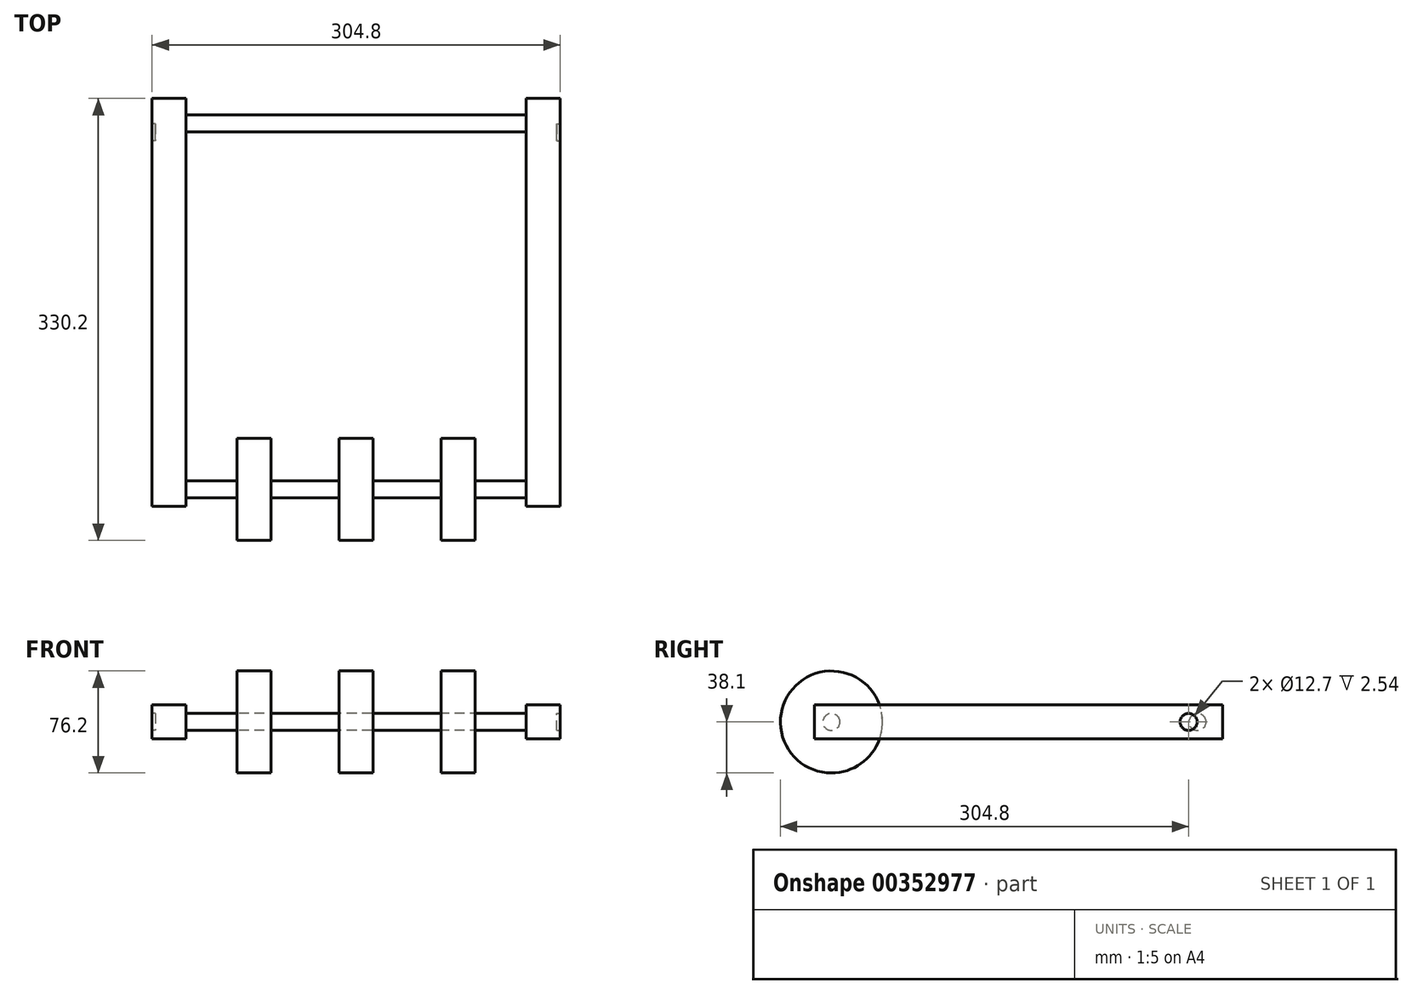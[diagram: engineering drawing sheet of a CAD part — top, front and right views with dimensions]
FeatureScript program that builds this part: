
annotation { "Feature Type Name" : "Feature", "Feature Type Description" : "" }
export const myFeature = defineFeature(function(context is Context, id is Id, definition is map)
    precondition{}
    {
        {
            var Q0;
            Q0=qCreatedBy(makeId("Front.planeOp"),FACE);
            var sketch = newSketch(context, id + "F0", { "sketchPlane" : qUnion([Q0])});
            skLineSegment(sketch, "E0.bottom", {"start": v(-127, -12.7) * mm, "end": v(-152.4, -12.7) * mm});
            skLineSegment(sketch, "E0.top", {"start": v(-127, 12.7) * mm, "end": v(-152.4, 12.7) * mm});
            skLineSegment(sketch, "E0.left", {"start": v(-127, -12.7) * mm, "end": v(-127, 12.7) * mm});
            skLineSegment(sketch, "E0.right", {"start": v(-152.4, -12.7) * mm, "end": v(-152.4, 12.7) * mm});
            skPoint(sketch, "E0.middle", {"position": v(-139.7, 0) * mm});
            skLineSegment(sketch, "E1.bottom", {"start": v(152.4, -12.7) * mm, "end": v(127, -12.7) * mm});
            skLineSegment(sketch, "E1.top", {"start": v(152.4, 12.7) * mm, "end": v(127, 12.7) * mm});
            skLineSegment(sketch, "E1.left", {"start": v(152.4, -12.7) * mm, "end": v(152.4, 12.7) * mm});
            skLineSegment(sketch, "E1.right", {"start": v(127, -12.7) * mm, "end": v(127, 12.7) * mm});
            skPoint(sketch, "E1.middle", {"position": v(139.7, 0) * mm});
            skSolve(sketch);
        }
        {
            var Q0;
            Q0 = qSketchRegion(id + "F0", true);
            extrude(context, id + "F1", {"entities" : qUnion([Q0]), "oppositeDirection" : true, "depth" : 25.4 * mm, "hasSecondDirection" : true, "secondDirectionOppositeDirection" : false, "secondDirectionDepth" : 279.4 * mm});
        }
        {
            var Q0;
            Q0=makeQuery(id+"F1.opExtrude","SWEPT_FACE",FACE,{"disambiguationData":[OSD([sQuery(id+"F0.wireOp",EDGE,"E0.right")])]});
            var sketch = newSketch(context, id + "F2", { "sketchPlane" : qUnion([Q0])});
            skCircle(sketch, "E2", {"center": v(0, 0) * mm, "radius": 6.35 * mm});
            skSolve(sketch);
        }
        {
            var Q0;
            Q0=makeQuery(id+"F1.opExtrude","SWEPT_FACE",FACE,{"disambiguationData":[OSD([sQuery(id+"F0.wireOp",EDGE,"E1.left")])]});
            var sketch = newSketch(context, id + "F3", { "sketchPlane" : qUnion([Q0])});
            skCircle(sketch, "E3", {"center": v(0, 0) * mm, "radius": 6.35 * mm});
            skSolve(sketch);
        }
        {
            var Q0;
            Q0 = qSketchRegion(id + "F2", true);
            extrude(context, id + "F4", {"entities" : qUnion([Q0]), "operationType" : NewBodyOperationType.REMOVE, "oppositeDirection" : true, "depth" : 2.54 * mm});
        }
        {
            var Q0;
            Q0 = qSketchRegion(id + "F3", true);
            extrude(context, id + "F5", {"entities" : qUnion([Q0]), "operationType" : NewBodyOperationType.REMOVE, "oppositeDirection" : true, "depth" : 2.54 * mm});
        }
        {
            var Q0;
            Q0=makeQuery(id+"F1.opExtrude","SWEPT_FACE",FACE,{"disambiguationData":[OSD([sQuery(id+"F0.wireOp",EDGE,"E0.left")])]});
            var sketch = newSketch(context, id + "F6", { "sketchPlane" : qUnion([Q0])});
            skCircle(sketch, "E4", {"center": v(6.7, 0) * mm, "radius": 6.35 * mm});
            skSolve(sketch);
        }
        {
            var Q0;
            Q0 = qSketchRegion(id + "F6", true);
            extrude(context, id + "F7", {"entities" : qUnion([Q0]), "depth" : 254 * mm});
        }
        {
            var Q0;
            Q0=makeQuery(id+"F1.opExtrude","SWEPT_FACE",FACE,{"disambiguationData":[OSD([sQuery(id+"F0.wireOp",EDGE,"E0.left")])]});
            var sketch = newSketch(context, id + "F8", { "sketchPlane" : qUnion([Q0])});
            skCircle(sketch, "E5", {"center": v(-266.7, 0) * mm, "radius": 6.35 * mm});
            skSolve(sketch);
        }
        {
            var Q0;
            Q0 = qSketchRegion(id + "F8", true);
            extrude(context, id + "F9", {"entities" : qUnion([Q0]), "depth" : 254 * mm});
        }
        {
            var Q0;
            Q0=qCreatedBy(makeId("Right.planeOp"),FACE);
            var sketch = newSketch(context, id + "F10", { "sketchPlane" : qUnion([Q0])});
            skCircle(sketch, "E6", {"center": v(-266.7, 0) * mm, "radius": 38.1 * mm});
            skSolve(sketch);
        }
        {
            var Q0;
            Q0 = qSketchRegion(id + "F10", true);
            extrude(context, id + "F11", {"entities" : qUnion([Q0]), "operationType" : NewBodyOperationType.ADD, "depth" : 88.9 * mm, "hasSecondDirection" : true, "secondDirectionOppositeDirection" : false, "secondDirectionDepth" : 63.5 * mm});
        }
        {
            var Q0;
            Q0=qCreatedBy(makeId("Right.planeOp"),FACE);
            var sketch = newSketch(context, id + "F12", { "sketchPlane" : qUnion([Q0])});
            skCircle(sketch, "E7", {"center": v(-266.7, 0) * mm, "radius": 38.1 * mm});
            skSolve(sketch);
        }
        {
            var Q0;
            Q0 = qSketchRegion(id + "F12", true);
            extrude(context, id + "F13", {"entities" : qUnion([Q0]), "operationType" : NewBodyOperationType.ADD, "oppositeDirection" : true, "depth" : 88.9 * mm, "hasSecondDirection" : true, "secondDirectionOppositeDirection" : true, "secondDirectionDepth" : 63.5 * mm});
        }
        {
            var Q0;
            Q0=qCreatedBy(makeId("Right.planeOp"),FACE);
            var sketch = newSketch(context, id + "F14", { "sketchPlane" : qUnion([Q0])});
            skCircle(sketch, "E8", {"center": v(-266.7, 0) * mm, "radius": 38.1 * mm});
            skSolve(sketch);
        }
        {
            var Q0;
            Q0 = qSketchRegion(id + "F14", true);
            extrude(context, id + "F15", {"entities" : qUnion([Q0]), "operationType" : NewBodyOperationType.ADD, "depth" : 12.7 * mm, "hasSecondDirection" : true, "secondDirectionOppositeDirection" : true, "secondDirectionDepth" : 12.7 * mm});
        }
    });
